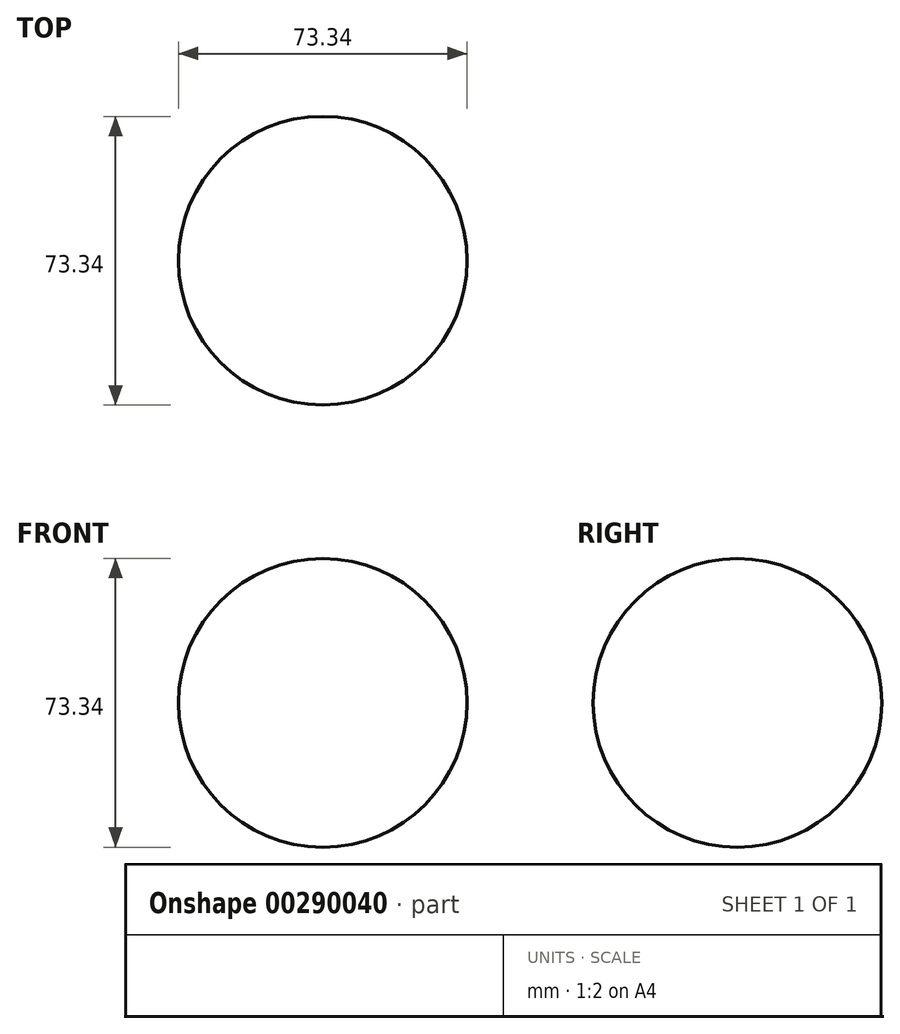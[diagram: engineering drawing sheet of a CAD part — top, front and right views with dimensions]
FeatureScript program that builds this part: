
annotation { "Feature Type Name" : "Feature", "Feature Type Description" : "" }
export const myFeature = defineFeature(function(context is Context, id is Id, definition is map)
    precondition{}
    {
        {
            var Q0;
            Q0=qCreatedBy(makeId("Front.planeOp"),FACE);
            var sketch = newSketch(context, id + "F0", { "sketchPlane" : qUnion([Q0])});
            skArc(sketch, "E0", {"start": v(0, -36.67) * mm, "mid": v(36.67, 0) * mm, "end": v(0, 36.67) * mm});
            skLineSegment(sketch, "E1", {"start": v(0, 36.67) * mm, "end": v(0, -36.67) * mm});
            skSolve(sketch);
        }
        {
            var Q0;
            Q0 = qSketchRegion(id + "F0", true);
            var Q1;
            Q1=sQuery(id+"F0.wireOp",EDGE,"E1");
            revolve(context, id + "F1", {"entities" : qUnion([Q0]), "axis" : qUnion([Q1]), "revolveType" : RevolveType.FULL});
        }
    });
